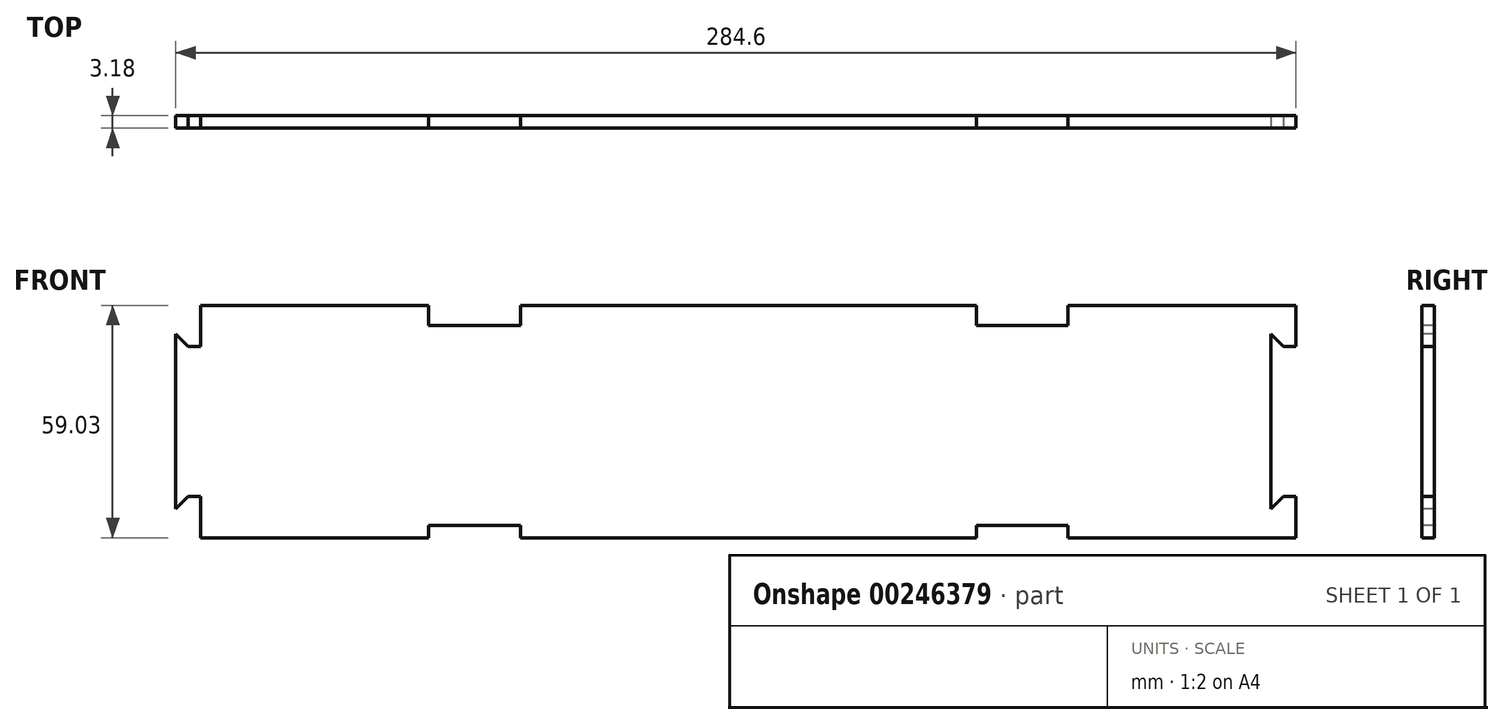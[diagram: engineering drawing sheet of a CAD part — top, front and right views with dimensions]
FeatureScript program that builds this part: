
annotation { "Feature Type Name" : "Feature", "Feature Type Description" : "" }
export const myFeature = defineFeature(function(context is Context, id is Id, definition is map)
    precondition{}
    {
        {
            var Q0;
            Q0=qCreatedBy(makeId("Front.planeOp"),FACE);
            var sketch = newSketch(context, id + "F0", { "sketchPlane" : qUnion([Q0])});
            skLineSegment(sketch, "E0.bottom", {"start": v(0, 0) * mm, "end": v(278.25, 0) * mm});
            skLineSegment(sketch, "E0.top", {"start": v(0, 50.8) * mm, "end": v(278.25, 50.8) * mm});
            skLineSegment(sketch, "E0.left", {"start": v(0, 0) * mm, "end": v(0, 50.8) * mm});
            skLineSegment(sketch, "E0.right", {"start": v(278.25, 0) * mm, "end": v(278.25, 50.8) * mm});
            skSolve(sketch);
        }
        {
            var Q0;
            Q0=makeQuery(id+"F0.imprint","IMPRINT",FACE,{"disambiguationData":[TD([[makeQuery(id+"F0.imprint","IMPRINT",EDGE,{"derivedFrom":sQuery(id+"F0.wireOp",EDGE,"E0.bottom")}),1.0]])]});
            extrude(context, id + "F1", {"entities" : qUnion([Q0]), "depth" : 3.17 * mm});
        }
        {
            var Q0;
            Q0=makeQuery(id+"F1.opExtrude","CAP_FACE",FACE,{"disambiguationData":[OSD([sQuery(id+"F0.wireOp",EDGE,"E0.bottom"),sQuery(id+"F0.wireOp",EDGE,"E0.top"),sQuery(id+"F0.wireOp",EDGE,"E0.left"),sQuery(id+"F0.wireOp",EDGE,"E0.right")])],"isStart":false});
            var sketch = newSketch(context, id + "F2", { "sketchPlane" : qUnion([Q0])});
            skLineSegment(sketch, "E1.bottom", {"start": v(0, 50.8) * mm, "end": v(57.92, 50.8) * mm});
            skLineSegment(sketch, "E1.top", {"start": v(0, 55.88) * mm, "end": v(57.92, 55.88) * mm});
            skLineSegment(sketch, "E1.left", {"start": v(0, 50.8) * mm, "end": v(0, 55.88) * mm});
            skLineSegment(sketch, "E1.right", {"start": v(57.92, 50.8) * mm, "end": v(57.92, 55.88) * mm});
            skLineSegment(sketch, "E2.bottom", {"start": v(81.2, 50.8) * mm, "end": v(197.05, 50.8) * mm});
            skLineSegment(sketch, "E2.top", {"start": v(81.2, 55.88) * mm, "end": v(197.05, 55.88) * mm});
            skLineSegment(sketch, "E2.left", {"start": v(81.2, 50.8) * mm, "end": v(81.2, 55.88) * mm});
            skLineSegment(sketch, "E2.right", {"start": v(197.05, 50.8) * mm, "end": v(197.05, 55.88) * mm});
            skLineSegment(sketch, "E3.bottom", {"start": v(220.32, 50.8) * mm, "end": v(278.25, 50.8) * mm});
            skLineSegment(sketch, "E3.top", {"start": v(220.32, 55.88) * mm, "end": v(278.25, 55.88) * mm});
            skLineSegment(sketch, "E3.left", {"start": v(220.32, 50.8) * mm, "end": v(220.32, 55.88) * mm});
            skLineSegment(sketch, "E3.right", {"start": v(278.25, 50.8) * mm, "end": v(278.25, 55.88) * mm});
            skLineSegment(sketch, "E4.bottom", {"start": v(0, 0) * mm, "end": v(57.92, 0) * mm});
            skLineSegment(sketch, "E4.top", {"start": v(0, -3.15) * mm, "end": v(57.92, -3.15) * mm});
            skLineSegment(sketch, "E4.left", {"start": v(0, 0) * mm, "end": v(0, -3.15) * mm});
            skLineSegment(sketch, "E4.right", {"start": v(57.92, 0) * mm, "end": v(57.92, -3.15) * mm});
            skLineSegment(sketch, "E5.bottom", {"start": v(81.2, 0) * mm, "end": v(197.05, 0) * mm});
            skLineSegment(sketch, "E5.top", {"start": v(81.2, -3.15) * mm, "end": v(197.05, -3.15) * mm});
            skLineSegment(sketch, "E5.left", {"start": v(81.2, 0) * mm, "end": v(81.2, -3.15) * mm});
            skLineSegment(sketch, "E5.right", {"start": v(197.05, 0) * mm, "end": v(197.05, -3.15) * mm});
            skLineSegment(sketch, "E6.bottom", {"start": v(278.25, 0) * mm, "end": v(220.32, 0) * mm});
            skLineSegment(sketch, "E6.top", {"start": v(278.25, -3.15) * mm, "end": v(220.32, -3.15) * mm});
            skLineSegment(sketch, "E6.left", {"start": v(278.25, 0) * mm, "end": v(278.25, -3.15) * mm});
            skLineSegment(sketch, "E6.right", {"start": v(220.32, 0) * mm, "end": v(220.32, -3.15) * mm});
            skSolve(sketch);
        }
        {
            var Q0;
            Q0=qSketchRegion(id+"F2",true);
            extrude(context, id + "F3", {"entities" : qUnion([Q0]), "operationType" : NewBodyOperationType.ADD, "oppositeDirection" : true, "depth" : 3.17 * mm});
        }
        {
            var Q0;
            Q0=makeQuery(id+"F3.boolean.opBoolean","MERGE",FACE,{"derivedFrom":[makeQuery(id+"F1.opExtrude","CAP_FACE",FACE,{"disambiguationData":[OSD([sQuery(id+"F0.wireOp",EDGE,"E0.bottom"),sQuery(id+"F0.wireOp",EDGE,"E0.top"),sQuery(id+"F0.wireOp",EDGE,"E0.left"),sQuery(id+"F0.wireOp",EDGE,"E0.right")])],"isStart":false}),makeQuery(id+"F3.opExtrude","CAP_FACE",FACE,{"disambiguationData":[OSD([sQuery(id+"F2.wireOp",EDGE,"yGTzQ0Go-BQov-uew2-KNTh-F3ipd09nucIb.bottom"),sQuery(id+"F2.wireOp",EDGE,"yGTzQ0Go-BQov-uew2-KNTh-F3ipd09nucIb.top"),sQuery(id+"F2.wireOp",EDGE,"yGTzQ0Go-BQov-uew2-KNTh-F3ipd09nucIb.left"),sQuery(id+"F2.wireOp",EDGE,"yGTzQ0Go-BQov-uew2-KNTh-F3ipd09nucIb.right")])],"isStart":true}),makeQuery(id+"F3.opExtrude","CAP_FACE",FACE,{"disambiguationData":[OSD([sQuery(id+"F2.wireOp",EDGE,"wki2vl1U-g3EK-wNWS-Wy9e-8S2yKaLzFqYa.bottom"),sQuery(id+"F2.wireOp",EDGE,"wki2vl1U-g3EK-wNWS-Wy9e-8S2yKaLzFqYa.top"),sQuery(id+"F2.wireOp",EDGE,"wki2vl1U-g3EK-wNWS-Wy9e-8S2yKaLzFqYa.left"),sQuery(id+"F2.wireOp",EDGE,"wki2vl1U-g3EK-wNWS-Wy9e-8S2yKaLzFqYa.right")])],"isStart":true}),makeQuery(id+"F3.opExtrude","CAP_FACE",FACE,{"disambiguationData":[OSD([sQuery(id+"F2.wireOp",EDGE,"LLAE6Vqy-DEZt-2peG-CHDM-G7Cv4obvmDhg.bottom"),sQuery(id+"F2.wireOp",EDGE,"LLAE6Vqy-DEZt-2peG-CHDM-G7Cv4obvmDhg.top"),sQuery(id+"F2.wireOp",EDGE,"LLAE6Vqy-DEZt-2peG-CHDM-G7Cv4obvmDhg.left"),sQuery(id+"F2.wireOp",EDGE,"LLAE6Vqy-DEZt-2peG-CHDM-G7Cv4obvmDhg.right")])],"isStart":true}),makeQuery(id+"F3.opExtrude","CAP_FACE",FACE,{"disambiguationData":[OSD([sQuery(id+"F2.wireOp",EDGE,"7tSHTBLr-E8Mj-zah7-gvYQ-b3FVimwfmpg8.bottom"),sQuery(id+"F2.wireOp",EDGE,"7tSHTBLr-E8Mj-zah7-gvYQ-b3FVimwfmpg8.top"),sQuery(id+"F2.wireOp",EDGE,"7tSHTBLr-E8Mj-zah7-gvYQ-b3FVimwfmpg8.left"),sQuery(id+"F2.wireOp",EDGE,"7tSHTBLr-E8Mj-zah7-gvYQ-b3FVimwfmpg8.right")])],"isStart":true}),makeQuery(id+"F3.opExtrude","CAP_FACE",FACE,{"disambiguationData":[OSD([sQuery(id+"F2.wireOp",EDGE,"5T6jGDGP-DRMR-oiqD-3d0M-ff0gA9U5u8ih.bottom"),sQuery(id+"F2.wireOp",EDGE,"5T6jGDGP-DRMR-oiqD-3d0M-ff0gA9U5u8ih.top"),sQuery(id+"F2.wireOp",EDGE,"5T6jGDGP-DRMR-oiqD-3d0M-ff0gA9U5u8ih.left"),sQuery(id+"F2.wireOp",EDGE,"5T6jGDGP-DRMR-oiqD-3d0M-ff0gA9U5u8ih.right")])],"isStart":true}),makeQuery(id+"F3.opExtrude","CAP_FACE",FACE,{"disambiguationData":[OSD([sQuery(id+"F2.wireOp",EDGE,"4sBa75E8-5JBT-rlAd-xXmu-v4jL8b3fPeIa.bottom"),sQuery(id+"F2.wireOp",EDGE,"4sBa75E8-5JBT-rlAd-xXmu-v4jL8b3fPeIa.top"),sQuery(id+"F2.wireOp",EDGE,"4sBa75E8-5JBT-rlAd-xXmu-v4jL8b3fPeIa.left"),sQuery(id+"F2.wireOp",EDGE,"4sBa75E8-5JBT-rlAd-xXmu-v4jL8b3fPeIa.right")])],"isStart":true}),makeQuery(id+"F3.opExtrude","CAP_FACE",FACE,{"disambiguationData":[OSD([sQuery(id+"F2.wireOp",EDGE,"D2wCNSyY-If53-1L5m-CG6f-jPf3mu9xeQZx.bottom"),sQuery(id+"F2.wireOp",EDGE,"D2wCNSyY-If53-1L5m-CG6f-jPf3mu9xeQZx.top"),sQuery(id+"F2.wireOp",EDGE,"D2wCNSyY-If53-1L5m-CG6f-jPf3mu9xeQZx.left"),sQuery(id+"F2.wireOp",EDGE,"D2wCNSyY-If53-1L5m-CG6f-jPf3mu9xeQZx.right")])],"isStart":true}),makeQuery(id+"F3.opExtrude","CAP_FACE",FACE,{"disambiguationData":[OSD([sQuery(id+"F2.wireOp",EDGE,"3nJxVRXX-auHE-NxEm-ef62-i3ycgrjordid.bottom"),sQuery(id+"F2.wireOp",EDGE,"3nJxVRXX-auHE-NxEm-ef62-i3ycgrjordid.top"),sQuery(id+"F2.wireOp",EDGE,"3nJxVRXX-auHE-NxEm-ef62-i3ycgrjordid.left"),sQuery(id+"F2.wireOp",EDGE,"3nJxVRXX-auHE-NxEm-ef62-i3ycgrjordid.right")])],"isStart":true})]});
            var sketch = newSketch(context, id + "F4", { "sketchPlane" : qUnion([Q0])});
            skLineSegment(sketch, "E7", {"start": v(0, 45.42) * mm, "end": v(-3.18, 45.42) * mm});
            skLineSegment(sketch, "E8", {"start": v(-3.18, 45.42) * mm, "end": v(-6.35, 48.6) * mm});
            skLineSegment(sketch, "E9", {"start": v(-6.35, 48.6) * mm, "end": v(-6.35, 4.14) * mm});
            skLineSegment(sketch, "E10", {"start": v(-6.35, 4.14) * mm, "end": v(-3.18, 7.32) * mm});
            skLineSegment(sketch, "E11", {"start": v(-3.18, 7.32) * mm, "end": v(0, 7.32) * mm});
            skLineSegment(sketch, "E12", {"start": v(278.25, 45.42) * mm, "end": v(275.07, 45.42) * mm});
            skLineSegment(sketch, "E13", {"start": v(275.07, 45.42) * mm, "end": v(271.9, 48.6) * mm});
            skLineSegment(sketch, "E14", {"start": v(271.9, 48.6) * mm, "end": v(271.9, 4.14) * mm});
            skLineSegment(sketch, "E15", {"start": v(271.9, 4.14) * mm, "end": v(275.07, 7.32) * mm});
            skLineSegment(sketch, "E16", {"start": v(275.07, 7.32) * mm, "end": v(278.25, 7.32) * mm});
            skPoint(sketch, "E17", {"position": v(0, 26.37) * mm});
            skPoint(sketch, "E18", {"position": v(-6.35, 26.37) * mm});
            skPoint(sketch, "E19", {"position": v(271.9, 26.37) * mm});
            skPoint(sketch, "E20", {"position": v(278.25, 26.37) * mm});
            skLineSegment(sketch, "E21", {"start": v(0, 45.42) * mm, "end": v(0, 7.32) * mm});
            skSolve(sketch);
        }
        {
            var Q0;
            Q0=makeQuery(id+"F4.imprint","IMPRINT",FACE,{"disambiguationData":[TD([[makeQuery(id+"F4.imprint","IMPRINT",EDGE,{"derivedFrom":sQuery(id+"F4.wireOp",EDGE,"E7")}),1.0]])]});
            extrude(context, id + "F5", {"entities" : qUnion([Q0]), "operationType" : NewBodyOperationType.ADD, "oppositeDirection" : true, "depth" : 3.17 * mm});
        }
        {
            var Q0;
            {var subQ0=sQuery(id+"F4.wireOp",EDGE,"E12");Q0=makeQuery(id+"F4.imprint","IMPRINT",FACE,{"disambiguationData":[TD([[makeQuery(id+"F4.imprint","IMPRINT",EDGE,{"derivedFrom":subQ0}),1.0]])]});}
            extrude(context, id + "F6", {"entities" : qUnion([Q0]), "operationType" : NewBodyOperationType.REMOVE, "endBound" : BoundingType.THROUGH_ALL, "oppositeDirection" : true, "depth" : 25.4 * mm});
        }
    });
